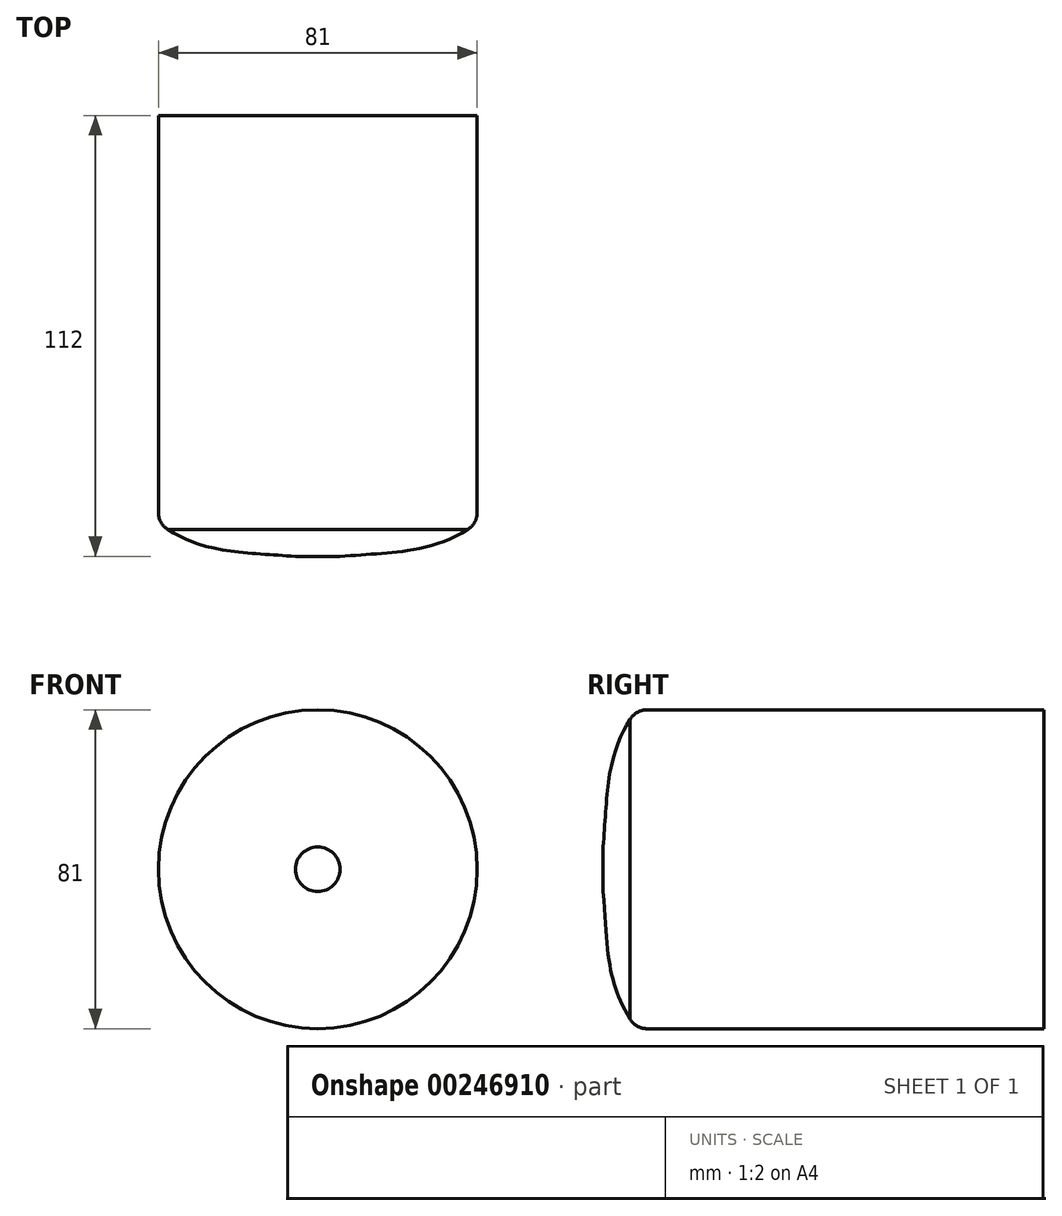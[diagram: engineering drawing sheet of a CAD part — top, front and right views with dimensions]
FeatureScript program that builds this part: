
annotation { "Feature Type Name" : "Feature", "Feature Type Description" : "" }
export const myFeature = defineFeature(function(context is Context, id is Id, definition is map)
    precondition{}
    {
        {
            var Q0;
            Q0=qCreatedBy(makeId("Top.planeOp"),FACE);
            var sketch = newSketch(context, id + "F0", { "sketchPlane" : qUnion([Q0])});
            skLineSegment(sketch, "E0", {"start": v(0, 0) * mm, "end": v(40.5, 0) * mm});
            skLineSegment(sketch, "E1", {"start": v(40.5, 0) * mm, "end": v(40.5, -103.65) * mm});
            skLineSegment(sketch, "E2", {"start": v(5.65, -112) * mm, "end": v(0, -112) * mm});
            skLineSegment(sketch, "E3", {"start": v(0, -112) * mm, "end": v(0, 0) * mm});
            skFitSpline(sketch, "E4", {"points": [v(40.5, -103.65) * mm, v(5.65, -112) * mm], "startDerivative": vector(-32.91, -21.16) * mm, "endDerivative": vector(-56.93, -3.88) * mm});
            skSolve(sketch);
        }
        {
            var Q0;
            Q0=makeQuery(id+"F0.imprint","IMPRINT",FACE,{"disambiguationData":[TD([[makeQuery(id+"F0.imprint","IMPRINT",EDGE,{"derivedFrom":sQuery(id+"F0.wireOp",EDGE,"E0")}),-1.0]])]});
            var Q1;
            Q1=sQuery(id+"F0.wireOp",EDGE,"E3");
            revolve(context, id + "F1", {"entities" : qUnion([Q0]), "axis" : qUnion([Q1]), "revolveType" : RevolveType.FULL});
        }
        {
            var Q0;
            Q0=makeQuery(id+"F1.opRevolve","SWEPT_EDGE",EDGE,{"disambiguationData":[OSD([sQuery(id+"F0.wireOp",EDGE,"E1"),sQuery(id+"F0.wireOp",EDGE,"E4")])]});
            fillet(context, id + "F2", {"entities" : qUnion([Q0]), "radius" : 5 * mm, "tangentPropagation" : true, "allowEdgeOverflow" : false});
        }
    });
